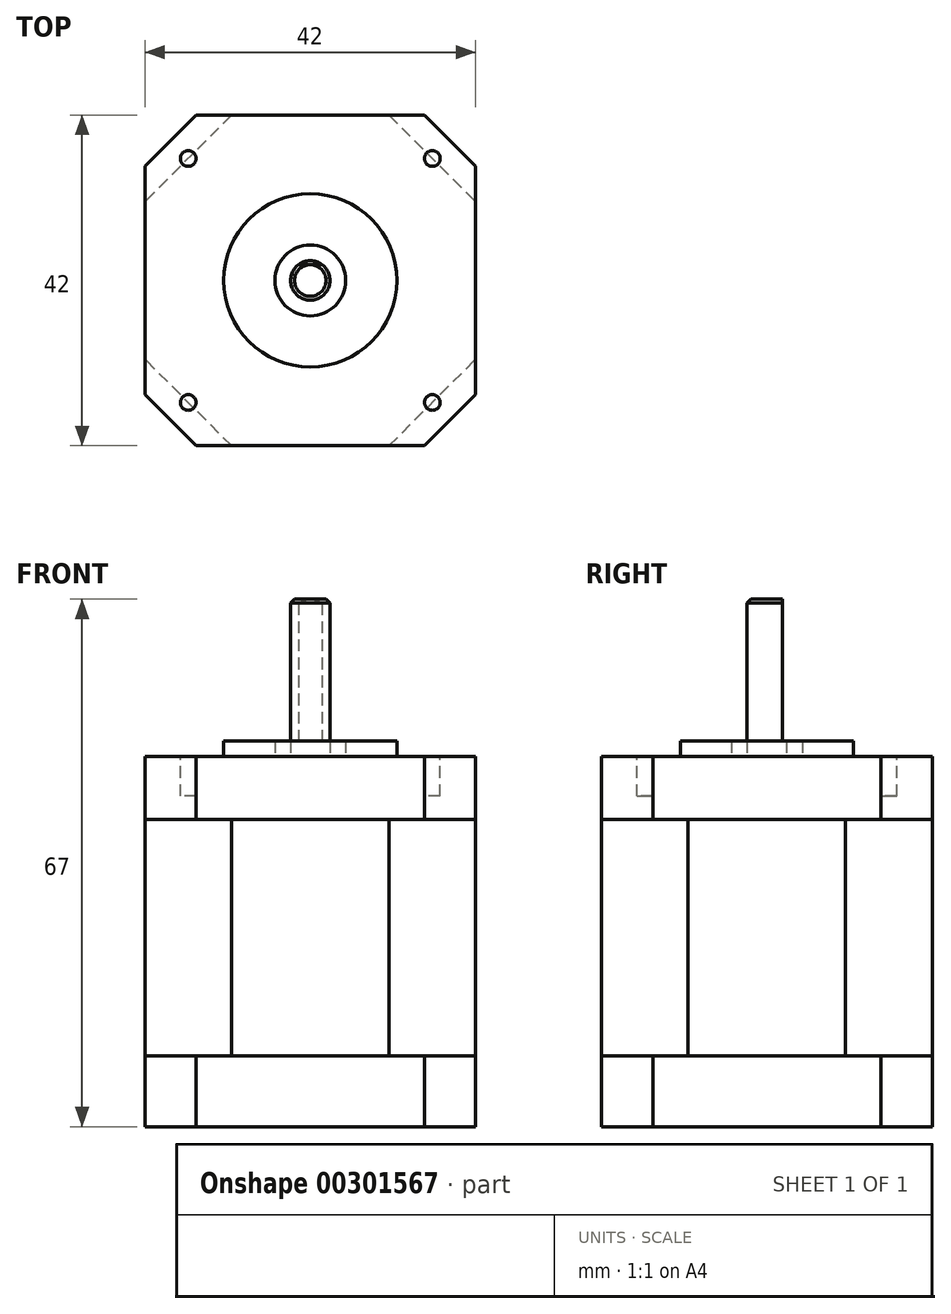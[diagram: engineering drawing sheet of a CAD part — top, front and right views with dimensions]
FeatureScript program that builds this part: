
annotation { "Feature Type Name" : "Feature", "Feature Type Description" : "" }
export const myFeature = defineFeature(function(context is Context, id is Id, definition is map)
    precondition{}
    {
        {
            var Q0;
            Q0=qCreatedBy(makeId("Top.planeOp"),FACE);
            var sketch = newSketch(context, id + "F0", { "sketchPlane" : qUnion([Q0])});
            skLineSegment(sketch, "E0.bottom", {"start": v(-21, 21) * mm, "end": v(21, 21) * mm});
            skLineSegment(sketch, "E0.top", {"start": v(-21, -21) * mm, "end": v(21, -21) * mm});
            skLineSegment(sketch, "E0.left", {"start": v(-21, 21) * mm, "end": v(-21, -21) * mm});
            skLineSegment(sketch, "E0.right", {"start": v(21, 21) * mm, "end": v(21, -21) * mm});
            skPoint(sketch, "E0.middle", {"position": v(0, 0) * mm});
            skSolve(sketch);
        }
        {
            var Q0;
            Q0=makeQuery(id+"F0.imprint","IMPRINT",FACE,{"disambiguationData":[TD([[makeQuery(id+"F0.imprint","IMPRINT",EDGE,{"derivedFrom":sQuery(id+"F0.wireOp",EDGE,"E0.bottom")}),-1.0]])]});
            extrude(context, id + "F1", {"entities" : qUnion([Q0]), "depth" : 9 * mm});
        }
        {
            var Q0;
            Q0=makeQuery(id+"F1.opExtrude","SWEPT_EDGE",EDGE,{"disambiguationData":[OSD([sQuery(id+"F0.wireOp",EDGE,"E0.top"),sQuery(id+"F0.wireOp",EDGE,"E0.left")])]});
            var Q1;
            Q1=makeQuery(id+"F1.opExtrude","SWEPT_EDGE",EDGE,{"disambiguationData":[OSD([sQuery(id+"F0.wireOp",EDGE,"E0.top"),sQuery(id+"F0.wireOp",EDGE,"E0.right")])]});
            var Q2;
            Q2=makeQuery(id+"F1.opExtrude","SWEPT_EDGE",EDGE,{"disambiguationData":[OSD([sQuery(id+"F0.wireOp",EDGE,"E0.bottom"),sQuery(id+"F0.wireOp",EDGE,"E0.right")])]});
            var Q3;
            Q3=makeQuery(id+"F1.opExtrude","SWEPT_EDGE",EDGE,{"disambiguationData":[OSD([sQuery(id+"F0.wireOp",EDGE,"E0.bottom"),sQuery(id+"F0.wireOp",EDGE,"E0.left")])]});
            chamfer(context, id + "F2", {"entities" : qUnion([Q0, Q1, Q2, Q3]), "width" : 6.5 * mm, "tangentPropagation" : true});
        }
        {
            var Q0;
            Q0=makeQuery(id+"F1.opExtrude","CAP_FACE",FACE,{"disambiguationData":[OSD([sQuery(id+"F0.wireOp",EDGE,"E0.bottom"),sQuery(id+"F0.wireOp",EDGE,"E0.top"),sQuery(id+"F0.wireOp",EDGE,"E0.left"),sQuery(id+"F0.wireOp",EDGE,"E0.right")])],"isStart":false});
            var sketch = newSketch(context, id + "F3", { "sketchPlane" : qUnion([Q0])});
            skLineSegment(sketch, "E1.bottom", {"start": v(-21, 21) * mm, "end": v(21, 21) * mm});
            skLineSegment(sketch, "E1.top", {"start": v(-21, -21) * mm, "end": v(21, -21) * mm});
            skLineSegment(sketch, "E1.left", {"start": v(-21, 21) * mm, "end": v(-21, -21) * mm});
            skLineSegment(sketch, "E1.right", {"start": v(21, 21) * mm, "end": v(21, -21) * mm});
            skPoint(sketch, "E1.middle", {"position": v(0, 0) * mm});
            skSolve(sketch);
        }
        {
            var Q0;
            Q0=qSketchRegion(id+"F3",true);
            extrude(context, id + "F4", {"entities" : qUnion([Q0]), "depth" : 30 * mm});
        }
        {
            var Q0;
            Q0=makeQuery(id+"F4.opExtrude","SWEPT_EDGE",EDGE,{"disambiguationData":[OSD([sQuery(id+"F3.wireOp",EDGE,"E1.bottom"),sQuery(id+"F3.wireOp",EDGE,"E1.right")])]});
            var Q1;
            Q1=makeQuery(id+"F4.opExtrude","SWEPT_EDGE",EDGE,{"disambiguationData":[OSD([sQuery(id+"F3.wireOp",EDGE,"E1.bottom"),sQuery(id+"F3.wireOp",EDGE,"E1.left")])]});
            var Q2;
            Q2=makeQuery(id+"F4.opExtrude","SWEPT_EDGE",EDGE,{"disambiguationData":[OSD([sQuery(id+"F3.wireOp",EDGE,"E1.top"),sQuery(id+"F3.wireOp",EDGE,"E1.left")])]});
            var Q3;
            Q3=makeQuery(id+"F4.opExtrude","SWEPT_EDGE",EDGE,{"disambiguationData":[OSD([sQuery(id+"F3.wireOp",EDGE,"E1.top"),sQuery(id+"F3.wireOp",EDGE,"E1.right")])]});
            chamfer(context, id + "F5", {"entities" : qUnion([Q0, Q1, Q2, Q3]), "width" : 11 * mm, "tangentPropagation" : true});
        }
        {
            var Q0;
            Q0=makeQuery(id+"F4.opExtrude","CAP_FACE",FACE,{"disambiguationData":[OSD([sQuery(id+"F3.wireOp",EDGE,"E1.bottom"),sQuery(id+"F3.wireOp",EDGE,"E1.top"),sQuery(id+"F3.wireOp",EDGE,"E1.left"),sQuery(id+"F3.wireOp",EDGE,"E1.right")])],"isStart":false});
            var sketch = newSketch(context, id + "F6", { "sketchPlane" : qUnion([Q0])});
            skLineSegment(sketch, "E2.bottom", {"start": v(21, 21) * mm, "end": v(-21, 21) * mm});
            skLineSegment(sketch, "E2.top", {"start": v(21, -21) * mm, "end": v(-21, -21) * mm});
            skLineSegment(sketch, "E2.left", {"start": v(21, 21) * mm, "end": v(21, -21) * mm});
            skLineSegment(sketch, "E2.right", {"start": v(-21, 21) * mm, "end": v(-21, -21) * mm});
            skPoint(sketch, "E2.middle", {"position": v(0, 0) * mm});
            skSolve(sketch);
        }
        {
            var Q0;
            Q0=qSketchRegion(id+"F6",true);
            extrude(context, id + "F7", {"entities" : qUnion([Q0]), "depth" : 8 * mm});
        }
        {
            var Q0;
            Q0=makeQuery(id+"F7.opExtrude","SWEPT_EDGE",EDGE,{"disambiguationData":[OSD([sQuery(id+"F6.wireOp",EDGE,"E2.top"),sQuery(id+"F6.wireOp",EDGE,"E2.right")])]});
            var Q1;
            Q1=makeQuery(id+"F7.opExtrude","SWEPT_EDGE",EDGE,{"disambiguationData":[OSD([sQuery(id+"F6.wireOp",EDGE,"E2.top"),sQuery(id+"F6.wireOp",EDGE,"E2.left")])]});
            var Q2;
            Q2=makeQuery(id+"F7.opExtrude","SWEPT_EDGE",EDGE,{"disambiguationData":[OSD([sQuery(id+"F6.wireOp",EDGE,"E2.bottom"),sQuery(id+"F6.wireOp",EDGE,"E2.left")])]});
            var Q3;
            Q3=makeQuery(id+"F7.opExtrude","SWEPT_EDGE",EDGE,{"disambiguationData":[OSD([sQuery(id+"F6.wireOp",EDGE,"E2.bottom"),sQuery(id+"F6.wireOp",EDGE,"E2.right")])]});
            chamfer(context, id + "F8", {"entities" : qUnion([Q0, Q1, Q2, Q3]), "width" : 6.5 * mm, "tangentPropagation" : true});
        }
        {
            var Q0;
            Q0=makeQuery(id+"F7.opExtrude","CAP_FACE",FACE,{"disambiguationData":[OSD([sQuery(id+"F6.wireOp",EDGE,"E2.bottom"),sQuery(id+"F6.wireOp",EDGE,"E2.top"),sQuery(id+"F6.wireOp",EDGE,"E2.left"),sQuery(id+"F6.wireOp",EDGE,"E2.right")])],"isStart":false});
            var sketch = newSketch(context, id + "F9", { "sketchPlane" : qUnion([Q0])});
            skCircle(sketch, "E3", {"center": v(0, 0) * mm, "radius": 4.5 * mm});
            skCircle(sketch, "E4", {"center": v(0, 0) * mm, "radius": 11 * mm});
            skSolve(sketch);
        }
        {
            var Q0;
            Q0=makeQuery(id+"F9.imprint","IMPRINT",FACE,{"disambiguationData":[TD([[makeQuery(id+"F9.imprint","IMPRINT",EDGE,{"derivedFrom":sQuery(id+"F9.wireOp",EDGE,"E3")}),-1.0]])]});
            extrude(context, id + "F10", {"entities" : qUnion([Q0]), "operationType" : NewBodyOperationType.ADD, "depth" : 2 * mm});
        }
        {
            var Q0;
            Q0=makeQuery(id+"F10.boolean.opBoolean","SPLIT",FACE,{"disambiguationData":[TD([makeQuery(id+"F10.opExtrude","SWEPT_FACE",FACE,{"disambiguationData":[OSD([sQuery(id+"F9.wireOp",EDGE,"E3")])]})])],"derivedFrom":makeQuery(id+"F7.opExtrude","CAP_FACE",FACE,{"disambiguationData":[OSD([sQuery(id+"F6.wireOp",EDGE,"E2.bottom"),sQuery(id+"F6.wireOp",EDGE,"E2.top"),sQuery(id+"F6.wireOp",EDGE,"E2.left"),sQuery(id+"F6.wireOp",EDGE,"E2.right")])],"isStart":false})});
            var sketch = newSketch(context, id + "F11", { "sketchPlane" : qUnion([Q0])});
            skCircle(sketch, "E5", {"center": v(0, 0) * mm, "radius": 2.5 * mm});
            skSolve(sketch);
        }
        {
            var Q0;
            Q0=qSketchRegion(id+"F11",true);
            extrude(context, id + "F12", {"entities" : qUnion([Q0]), "depth" : 20 * mm});
        }
        {
            var Q0;
            Q0=makeQuery(id+"F12.opExtrude","CAP_EDGE",EDGE,{"disambiguationData":[OSD([sQuery(id+"F11.wireOp",EDGE,"E5")])],"isStart":false});
            chamfer(context, id + "F13", {"entities" : qUnion([Q0]), "width" : 0.5 * mm, "tangentPropagation" : true});
        }
        {
            var Q0;
            Q0=makeQuery(id+"F12.opExtrude","CAP_FACE",FACE,{"disambiguationData":[OSD([sQuery(id+"F11.wireOp",EDGE,"E5")])],"isStart":false});
            var sketch = newSketch(context, id + "F14", { "sketchPlane" : qUnion([Q0])});
            skLineSegment(sketch, "E6.bottom", {"start": v(-3, 2) * mm, "end": v(3, 2) * mm});
            skLineSegment(sketch, "E6.top", {"start": v(-3, 3) * mm, "end": v(3, 3) * mm});
            skLineSegment(sketch, "E6.left", {"start": v(-3, 2) * mm, "end": v(-3, 3) * mm});
            skLineSegment(sketch, "E6.right", {"start": v(3, 2) * mm, "end": v(3, 3) * mm});
            skPoint(sketch, "E6.middle", {"position": v(0, 2.5) * mm});
            skSolve(sketch);
        }
        {
            var Q0;
            Q0=qSketchRegion(id+"F14",true);
            extrude(context, id + "F15", {"entities" : qUnion([Q0]), "operationType" : NewBodyOperationType.REMOVE, "oppositeDirection" : true, "depth" : 18 * mm});
        }
        {
            var Q0;
            {var subQ0=sQuery(id+"F6.wireOp",EDGE,"E2.right");var subQ1=sQuery(id+"F6.wireOp",EDGE,"E2.bottom");var subQ2=sQuery(id+"F6.wireOp",EDGE,"E2.top");var subQ3=sQuery(id+"F6.wireOp",EDGE,"E2.left");Q0=makeQuery(id+"F10.boolean.opBoolean","SPLIT",FACE,{"disambiguationData":[TD([makeQuery(id+"F7.opExtrude","SWEPT_FACE",FACE,{"disambiguationData":[OSD([subQ1])]})])],"derivedFrom":makeQuery(id+"F7.opExtrude","CAP_FACE",FACE,{"disambiguationData":[OSD([subQ1,subQ2,subQ3,subQ0])],"isStart":false})});}
            var sketch = newSketch(context, id + "F16", { "sketchPlane" : qUnion([Q0])});
            skCircle(sketch, "E7", {"center": v(-15.5, 15.5) * mm, "radius": 1 * mm});
            skCircle(sketch, "E8.1.0.0", {"center": v(15.5, 15.5) * mm, "radius": 1 * mm});
            skLineSegment(sketch, "E8.direction1", {"start": v(-15.5, 15.5) * mm, "end": v(15.5, 15.5) * mm, "construction": true});
            skLineSegment(sketch, "E9", {"start": v(0, 15.5) * mm, "end": v(0, -15.5) * mm, "construction": true});
            skCircle(sketch, "E10", {"center": v(-15.5, -15.5) * mm, "radius": 1 * mm});
            skCircle(sketch, "E11.1.0.0", {"center": v(15.5, -15.5) * mm, "radius": 1 * mm});
            skLineSegment(sketch, "E11.direction1", {"start": v(-15.5, -15.5) * mm, "end": v(15.5, -15.5) * mm, "construction": true});
            skLineSegment(sketch, "E12", {"start": v(-15.5, 0) * mm, "end": v(25.62, 0) * mm, "construction": true});
            skPoint(sketch, "E12.endSnap0", {"position": v(21, 0) * mm});
            skSolve(sketch);
        }
        {
            var Q0;
            Q0=qSketchRegion(id+"F16",true);
            extrude(context, id + "F17", {"entities" : qUnion([Q0]), "operationType" : NewBodyOperationType.REMOVE, "oppositeDirection" : true, "depth" : 5 * mm});
        }
        {
            var Q0;
            Q0=qSketchRegion(id+"F14",true);
            extrude(context, id + "F18", {"entities" : qUnion([Q0]), "operationType" : NewBodyOperationType.REMOVE, "oppositeDirection" : true, "depth" : 17 * mm});
        }
    });
